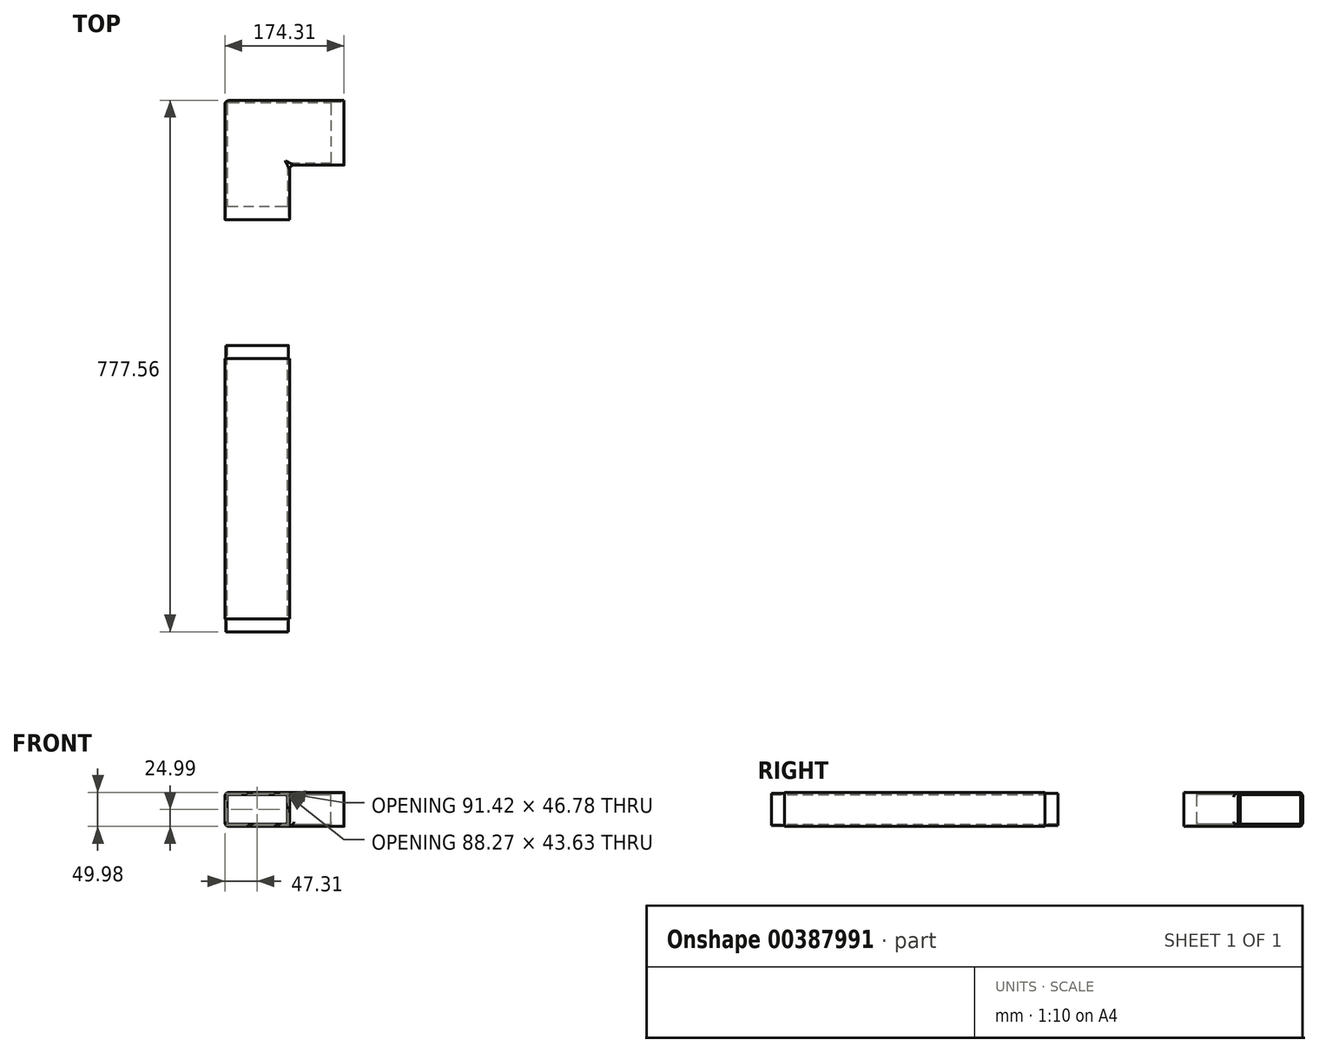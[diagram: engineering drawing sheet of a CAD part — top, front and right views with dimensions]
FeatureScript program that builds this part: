
annotation { "Feature Type Name" : "Feature", "Feature Type Description" : "" }
export const myFeature = defineFeature(function(context is Context, id is Id, definition is map)
    precondition{}
    {
        {
            var Q0;
            Q0=qCreatedBy(makeId("Front.planeOp"),FACE);
            var Q1;
            Q1=qCreatedBy(makeId("Right.planeOp"),FACE);
            cPlane(context, id + "F0", {"entities" : qUnion([Q0, Q1]), "cplaneType" : CPlaneType.MID_PLANE, "offset" : 25.4 * mm, "width" : 152.4 * mm, "height" : 152.4 * mm});
        }
        {
            var Q0;
            Q0=qCreatedBy(makeId("Right.planeOp"),FACE);
            cPlane(context, id + "F1", {"entities" : qUnion([Q0]), "cplaneType" : CPlaneType.OFFSET, "offset" : 127 * mm, "width" : 152.4 * mm, "height" : 152.4 * mm});
        }
        {
            var Q0;
            Q0=qCreatedBy(makeId("Front.planeOp"),FACE);
            cPlane(context, id + "F2", {"entities" : qUnion([Q0]), "cplaneType" : CPlaneType.OFFSET, "offset" : 127 * mm, "width" : 152.4 * mm, "height" : 152.4 * mm});
        }
        {
            var Q0;
            Q0=qCreatedBy(id+"F2.planeOp",FACE);
            var sketch = newSketch(context, id + "F3", { "sketchPlane" : qUnion([Q0])});
            skLineSegment(sketch, "E0.bottom", {"start": v(40.96, -24.99) * mm, "end": v(-40.96, -24.99) * mm});
            skLineSegment(sketch, "E0.top", {"start": v(40.96, 24.99) * mm, "end": v(-40.96, 24.99) * mm});
            skLineSegment(sketch, "E0.left", {"start": v(47.31, -18.64) * mm, "end": v(47.31, 18.64) * mm});
            skLineSegment(sketch, "E0.right", {"start": v(-47.31, -18.64) * mm, "end": v(-47.31, 18.64) * mm});
            skLineSegment(sketch, "E1.0", {"start": v(40.96, 21.81) * mm, "end": v(-40.96, 21.81) * mm});
            skLineSegment(sketch, "E1.1", {"start": v(44.14, -18.64) * mm, "end": v(44.14, 18.64) * mm});
            skLineSegment(sketch, "E1.2", {"start": v(40.96, -21.81) * mm, "end": v(-40.96, -21.81) * mm});
            skLineSegment(sketch, "E1.3", {"start": v(-44.14, -18.64) * mm, "end": v(-44.14, 18.64) * mm});
            skArc(sketch, "E2.filletArc", {"start": v(-40.96, 21.81) * mm, "mid": v(-43.2, 20.88) * mm, "end": v(-44.14, 18.64) * mm});
            skArc(sketch, "E3.filletArc", {"start": v(-44.14, -18.64) * mm, "mid": v(-43.2, -20.88) * mm, "end": v(-40.96, -21.81) * mm});
            skArc(sketch, "E4.filletArc", {"start": v(44.14, 18.64) * mm, "mid": v(43.2, 20.88) * mm, "end": v(40.96, 21.81) * mm});
            skArc(sketch, "E5.filletArc", {"start": v(40.96, -21.81) * mm, "mid": v(43.2, -20.88) * mm, "end": v(44.14, -18.64) * mm});
            skArc(sketch, "E6.filletArc", {"start": v(47.31, 18.64) * mm, "mid": v(45.45, 23.13) * mm, "end": v(40.96, 24.99) * mm});
            skArc(sketch, "E7.filletArc", {"start": v(40.96, -24.99) * mm, "mid": v(45.45, -23.13) * mm, "end": v(47.31, -18.64) * mm});
            skArc(sketch, "E8.filletArc", {"start": v(-47.31, -18.64) * mm, "mid": v(-45.45, -23.13) * mm, "end": v(-40.96, -24.99) * mm});
            skArc(sketch, "E9.filletArc", {"start": v(-40.96, 24.99) * mm, "mid": v(-45.45, 23.13) * mm, "end": v(-47.31, 18.64) * mm});
            skSolve(sketch);
        }
        {
            var Q0;
            Q0=qCreatedBy(id+"F1.planeOp",FACE);
            var sketch = newSketch(context, id + "F4", { "sketchPlane" : qUnion([Q0])});
            skLineSegment(sketch, "E10.bottom", {"start": v(40.96, -24.99) * mm, "end": v(-40.96, -24.99) * mm});
            skLineSegment(sketch, "E10.top", {"start": v(40.96, 24.99) * mm, "end": v(-40.96, 24.99) * mm});
            skLineSegment(sketch, "E10.left", {"start": v(47.31, -18.64) * mm, "end": v(47.31, 18.64) * mm});
            skLineSegment(sketch, "E10.right", {"start": v(-47.31, -18.64) * mm, "end": v(-47.31, 18.64) * mm});
            skLineSegment(sketch, "E11.0", {"start": v(40.96, 21.81) * mm, "end": v(-40.96, 21.81) * mm});
            skLineSegment(sketch, "E11.1", {"start": v(44.14, -18.64) * mm, "end": v(44.14, 18.64) * mm});
            skLineSegment(sketch, "E11.2", {"start": v(40.96, -21.81) * mm, "end": v(-40.96, -21.81) * mm});
            skLineSegment(sketch, "E11.3", {"start": v(-44.14, -18.64) * mm, "end": v(-44.14, 18.64) * mm});
            skArc(sketch, "E12.filletArc", {"start": v(-40.96, 21.81) * mm, "mid": v(-43.2, 20.88) * mm, "end": v(-44.14, 18.64) * mm});
            skArc(sketch, "E13.filletArc", {"start": v(-44.14, -18.64) * mm, "mid": v(-43.2, -20.88) * mm, "end": v(-40.96, -21.81) * mm});
            skArc(sketch, "E14.filletArc", {"start": v(44.14, 18.64) * mm, "mid": v(43.2, 20.88) * mm, "end": v(40.96, 21.81) * mm});
            skArc(sketch, "E15.filletArc", {"start": v(40.96, -21.81) * mm, "mid": v(43.2, -20.88) * mm, "end": v(44.14, -18.64) * mm});
            skArc(sketch, "E16.filletArc", {"start": v(47.31, 18.64) * mm, "mid": v(45.45, 23.13) * mm, "end": v(40.96, 24.99) * mm});
            skArc(sketch, "E17.filletArc", {"start": v(40.96, -24.99) * mm, "mid": v(45.45, -23.13) * mm, "end": v(47.31, -18.64) * mm});
            skArc(sketch, "E18.filletArc", {"start": v(-47.31, -18.64) * mm, "mid": v(-45.45, -23.13) * mm, "end": v(-40.96, -24.99) * mm});
            skArc(sketch, "E19.filletArc", {"start": v(-40.96, 24.99) * mm, "mid": v(-45.45, 23.13) * mm, "end": v(-47.31, 18.64) * mm});
            skSolve(sketch);
        }
        {
            var Q0;
            Q0 = qSketchRegion(id + "F3", true);
            var Q1;
            Q1=qCreatedBy(id+"F0.planeOp",FACE);
            extrude(context, id + "F5", {"entities" : qUnion([Q0]), "endBound" : BoundingType.UP_TO_SURFACE, "oppositeDirection" : true, "endBoundEntityFace" : qUnion([Q1]), "depth" : 25.4 * mm});
        }
        {
            var Q0;
            Q0 = qSketchRegion(id + "F4", true);
            var Q1;
            Q1=qCreatedBy(id+"F0.planeOp",FACE);
            extrude(context, id + "F6", {"entities" : qUnion([Q0]), "endBound" : BoundingType.UP_TO_SURFACE, "oppositeDirection" : true, "endBoundEntityFace" : qUnion([Q1]), "depth" : 25.4 * mm});
        }
        {
            var Q0;
            Q0=makeQuery(id+"F6.opExtrude","SWEPT_BODY",BODY,{"disambiguationData":[OSD([sQuery(id+"F4.wireOp",EDGE,"E10.bottom"),sQuery(id+"F4.wireOp",EDGE,"E10.top"),sQuery(id+"F4.wireOp",EDGE,"E10.left"),sQuery(id+"F4.wireOp",EDGE,"E10.right"),sQuery(id+"F4.wireOp",EDGE,"E11.0"),sQuery(id+"F4.wireOp",EDGE,"E11.1"),sQuery(id+"F4.wireOp",EDGE,"E11.2"),sQuery(id+"F4.wireOp",EDGE,"E11.3"),sQuery(id+"F4.wireOp",EDGE,"E12.filletArc"),sQuery(id+"F4.wireOp",EDGE,"E13.filletArc"),sQuery(id+"F4.wireOp",EDGE,"E14.filletArc"),sQuery(id+"F4.wireOp",EDGE,"E15.filletArc"),sQuery(id+"F4.wireOp",EDGE,"E16.filletArc"),sQuery(id+"F4.wireOp",EDGE,"E17.filletArc"),sQuery(id+"F4.wireOp",EDGE,"E18.filletArc"),sQuery(id+"F4.wireOp",EDGE,"E19.filletArc")])]});
            var Q1;
            Q1=makeQuery(id+"F5.opExtrude","SWEPT_BODY",BODY,{"disambiguationData":[OSD([sQuery(id+"F3.wireOp",EDGE,"E0.bottom"),sQuery(id+"F3.wireOp",EDGE,"E0.top"),sQuery(id+"F3.wireOp",EDGE,"E0.left"),sQuery(id+"F3.wireOp",EDGE,"E0.right"),sQuery(id+"F3.wireOp",EDGE,"E1.0"),sQuery(id+"F3.wireOp",EDGE,"E1.1"),sQuery(id+"F3.wireOp",EDGE,"E1.2"),sQuery(id+"F3.wireOp",EDGE,"E1.3"),sQuery(id+"F3.wireOp",EDGE,"E2.filletArc"),sQuery(id+"F3.wireOp",EDGE,"E3.filletArc"),sQuery(id+"F3.wireOp",EDGE,"E4.filletArc"),sQuery(id+"F3.wireOp",EDGE,"E5.filletArc"),sQuery(id+"F3.wireOp",EDGE,"E6.filletArc"),sQuery(id+"F3.wireOp",EDGE,"E7.filletArc"),sQuery(id+"F3.wireOp",EDGE,"E8.filletArc"),sQuery(id+"F3.wireOp",EDGE,"E9.filletArc")])]});
            booleanBodies(context, id + "F7", {"operationType" : BooleanOperationType.UNION, "tools" : qUnion([Q0, Q1])});
        }
        {
            var Q0;
            Q0=makeQuery(id+"F7.opBoolean","MERGE",EDGE,{"derivedFrom":[makeQuery(id+"F5.opExtrude","CAP_EDGE",EDGE,{"disambiguationData":[OSD([sQuery(id+"F3.wireOp",EDGE,"E0.right")])],"isStart":false}),makeQuery(id+"F6.opExtrude","CAP_EDGE",EDGE,{"disambiguationData":[OSD([sQuery(id+"F4.wireOp",EDGE,"E10.left")])],"isStart":false})]});
            fillet(context, id + "F8", {"entities" : qUnion([Q0]), "radius" : 6.35 * mm, "tangentPropagation" : true, "allowEdgeOverflow" : false});
        }
        {
            var Q0;
            Q0=makeQuery(id+"F7.opBoolean","MERGE",EDGE,{"derivedFrom":[makeQuery(id+"F5.opExtrude","CAP_EDGE",EDGE,{"disambiguationData":[OSD([sQuery(id+"F3.wireOp",EDGE,"E1.3")])],"isStart":false}),makeQuery(id+"F6.opExtrude","CAP_EDGE",EDGE,{"disambiguationData":[OSD([sQuery(id+"F4.wireOp",EDGE,"E11.1")])],"isStart":false})]});
            fillet(context, id + "F9", {"entities" : qUnion([Q0]), "radius" : 3.17 * mm, "tangentPropagation" : true, "allowEdgeOverflow" : false});
        }
        {
            var Q0;
            Q0=makeQuery(id+"F7.opBoolean","MERGE",EDGE,{"derivedFrom":[makeQuery(id+"F5.opExtrude","CAP_EDGE",EDGE,{"disambiguationData":[OSD([sQuery(id+"F3.wireOp",EDGE,"E0.left")])],"isStart":false}),makeQuery(id+"F6.opExtrude","CAP_EDGE",EDGE,{"disambiguationData":[OSD([sQuery(id+"F4.wireOp",EDGE,"E10.right")])],"isStart":false})]});
            fillet(context, id + "F10", {"entities" : qUnion([Q0]), "radius" : 6.35 * mm, "tangentPropagation" : true, "allowEdgeOverflow" : false});
        }
        {
            var Q0;
            Q0=makeQuery(id+"F7.opBoolean","MERGE",EDGE,{"derivedFrom":[makeQuery(id+"F5.opExtrude","CAP_EDGE",EDGE,{"disambiguationData":[OSD([sQuery(id+"F3.wireOp",EDGE,"E1.1")])],"isStart":false}),makeQuery(id+"F6.opExtrude","CAP_EDGE",EDGE,{"disambiguationData":[OSD([sQuery(id+"F4.wireOp",EDGE,"E11.3")])],"isStart":false})]});
            fillet(context, id + "F11", {"entities" : qUnion([Q0]), "radius" : 3.17 * mm, "tangentPropagation" : true, "allowEdgeOverflow" : false});
        }
        {
            var Q0;
            Q0=makeQuery(id+"F6.opExtrude","CAP_FACE",FACE,{"disambiguationData":[OSD([sQuery(id+"F4.wireOp",EDGE,"E10.bottom"),sQuery(id+"F4.wireOp",EDGE,"E10.top"),sQuery(id+"F4.wireOp",EDGE,"E10.left"),sQuery(id+"F4.wireOp",EDGE,"E10.right"),sQuery(id+"F4.wireOp",EDGE,"E11.0"),sQuery(id+"F4.wireOp",EDGE,"E11.1"),sQuery(id+"F4.wireOp",EDGE,"E11.2"),sQuery(id+"F4.wireOp",EDGE,"E11.3"),sQuery(id+"F4.wireOp",EDGE,"E12.filletArc"),sQuery(id+"F4.wireOp",EDGE,"E13.filletArc"),sQuery(id+"F4.wireOp",EDGE,"E14.filletArc"),sQuery(id+"F4.wireOp",EDGE,"E15.filletArc"),sQuery(id+"F4.wireOp",EDGE,"E16.filletArc"),sQuery(id+"F4.wireOp",EDGE,"E17.filletArc"),sQuery(id+"F4.wireOp",EDGE,"E18.filletArc"),sQuery(id+"F4.wireOp",EDGE,"E19.filletArc")])],"isStart":true});
            var sketch = newSketch(context, id + "F12", { "sketchPlane" : qUnion([Q0])});
            skLineSegment(sketch, "E20.0", {"start": v(40.96, 21.81) * mm, "end": v(-40.96, 21.81) * mm});
            skLineSegment(sketch, "E20.1", {"start": v(44.14, -18.64) * mm, "end": v(44.14, 18.64) * mm});
            skLineSegment(sketch, "E20.2", {"start": v(40.96, -21.81) * mm, "end": v(-40.96, -21.81) * mm});
            skLineSegment(sketch, "E20.3", {"start": v(-44.14, -18.64) * mm, "end": v(-44.14, 18.64) * mm});
            skArc(sketch, "E21.filletArc", {"start": v(-40.96, 21.81) * mm, "mid": v(-43.2, 20.88) * mm, "end": v(-44.14, 18.64) * mm});
            skArc(sketch, "E22.filletArc", {"start": v(-44.14, -18.64) * mm, "mid": v(-43.2, -20.88) * mm, "end": v(-40.96, -21.81) * mm});
            skArc(sketch, "E23.filletArc", {"start": v(44.14, 18.64) * mm, "mid": v(43.2, 20.88) * mm, "end": v(40.96, 21.81) * mm});
            skArc(sketch, "E24.filletArc", {"start": v(40.96, -21.81) * mm, "mid": v(43.2, -20.88) * mm, "end": v(44.14, -18.64) * mm});
            skArc(sketch, "E25.0", {"start": v(45.71, 18.64) * mm, "mid": v(44.32, 22) * mm, "end": v(40.96, 23.39) * mm});
            skLineSegment(sketch, "E25.1", {"start": v(45.71, -18.64) * mm, "end": v(45.71, 18.64) * mm});
            skLineSegment(sketch, "E25.2", {"start": v(40.96, 23.39) * mm, "end": v(-40.96, 23.39) * mm});
            skArc(sketch, "E25.3", {"start": v(40.96, -23.39) * mm, "mid": v(44.32, -22) * mm, "end": v(45.71, -18.64) * mm});
            skArc(sketch, "E25.4", {"start": v(-40.96, 23.39) * mm, "mid": v(-44.32, 22) * mm, "end": v(-45.71, 18.64) * mm});
            skLineSegment(sketch, "E25.5", {"start": v(-45.71, -18.64) * mm, "end": v(-45.71, 18.64) * mm});
            skArc(sketch, "E25.6", {"start": v(-45.71, -18.64) * mm, "mid": v(-44.32, -22) * mm, "end": v(-40.96, -23.39) * mm});
            skLineSegment(sketch, "E25.7", {"start": v(40.96, -23.39) * mm, "end": v(-40.96, -23.39) * mm});
            skSolve(sketch);
        }
        {
            var Q0;
            Q0=makeQuery(id+"F12.imprint","IMPRINT",FACE,{"disambiguationData":[TD([[makeQuery(id+"F12.imprint","IMPRINT",EDGE,{"derivedFrom":sQuery(id+"F12.wireOp",EDGE,"E20.0")}),-1.0]])]});
            var Q1;
            Q1=sQuery(id+"F12.wireOp",EDGE,"E20.0");
            var Q2;
            Q2=sQuery(id+"F12.wireOp",EDGE,"E20.1");
            var Q3;
            Q3=sQuery(id+"F12.wireOp",EDGE,"E20.2");
            var Q4;
            Q4=sQuery(id+"F12.wireOp",EDGE,"E20.3");
            var Q5;
            Q5=sQuery(id+"F12.wireOp",EDGE,"E21.filletArc");
            var Q6;
            Q6=sQuery(id+"F12.wireOp",EDGE,"E22.filletArc");
            var Q7;
            Q7=sQuery(id+"F12.wireOp",EDGE,"E23.filletArc");
            var Q8;
            Q8=sQuery(id+"F12.wireOp",EDGE,"E24.filletArc");
            var Q9;
            Q9=sQuery(id+"F12.wireOp",EDGE,"E25.0");
            var Q10;
            Q10=sQuery(id+"F12.wireOp",EDGE,"E25.1");
            var Q11;
            Q11=sQuery(id+"F12.wireOp",EDGE,"E25.2");
            var Q12;
            Q12=sQuery(id+"F12.wireOp",EDGE,"E25.3");
            var Q13;
            Q13=sQuery(id+"F12.wireOp",EDGE,"E25.4");
            var Q14;
            Q14=sQuery(id+"F12.wireOp",EDGE,"E25.5");
            var Q15;
            Q15=sQuery(id+"F12.wireOp",EDGE,"E25.6");
            var Q16;
            Q16=sQuery(id+"F12.wireOp",EDGE,"E25.7");
            extrude(context, id + "F13", {"entities" : qUnion([Q0]), "operationType" : NewBodyOperationType.REMOVE, "surfaceEntities" : qUnion([Q1, Q2, Q3, Q4, Q5, Q6, Q7, Q8, Q9, Q10, Q11, Q12, Q13, Q14, Q15, Q16]), "oppositeDirection" : true, "depth" : 19.05 * mm});
        }
        {
            var Q0;
            Q0=makeQuery(id+"F5.opExtrude","CAP_FACE",FACE,{"disambiguationData":[OSD([sQuery(id+"F3.wireOp",EDGE,"E0.bottom"),sQuery(id+"F3.wireOp",EDGE,"E0.top"),sQuery(id+"F3.wireOp",EDGE,"E0.left"),sQuery(id+"F3.wireOp",EDGE,"E0.right"),sQuery(id+"F3.wireOp",EDGE,"E1.0"),sQuery(id+"F3.wireOp",EDGE,"E1.1"),sQuery(id+"F3.wireOp",EDGE,"E1.2"),sQuery(id+"F3.wireOp",EDGE,"E1.3"),sQuery(id+"F3.wireOp",EDGE,"E2.filletArc"),sQuery(id+"F3.wireOp",EDGE,"E3.filletArc"),sQuery(id+"F3.wireOp",EDGE,"E4.filletArc"),sQuery(id+"F3.wireOp",EDGE,"E5.filletArc"),sQuery(id+"F3.wireOp",EDGE,"E6.filletArc"),sQuery(id+"F3.wireOp",EDGE,"E7.filletArc"),sQuery(id+"F3.wireOp",EDGE,"E8.filletArc"),sQuery(id+"F3.wireOp",EDGE,"E9.filletArc")])],"isStart":true});
            var sketch = newSketch(context, id + "F14", { "sketchPlane" : qUnion([Q0])});
            skArc(sketch, "E26.0", {"start": v(45.71, 18.64) * mm, "mid": v(44.32, 22) * mm, "end": v(40.96, 23.39) * mm});
            skLineSegment(sketch, "E26.1", {"start": v(45.71, -18.64) * mm, "end": v(45.71, 18.64) * mm});
            skLineSegment(sketch, "E26.2", {"start": v(40.96, 23.39) * mm, "end": v(-40.96, 23.39) * mm});
            skArc(sketch, "E26.3", {"start": v(40.96, -23.39) * mm, "mid": v(44.32, -22) * mm, "end": v(45.71, -18.64) * mm});
            skArc(sketch, "E26.4", {"start": v(-40.96, 23.39) * mm, "mid": v(-44.32, 22) * mm, "end": v(-45.71, 18.64) * mm});
            skLineSegment(sketch, "E26.5", {"start": v(-45.71, -18.64) * mm, "end": v(-45.71, 18.64) * mm});
            skArc(sketch, "E26.6", {"start": v(-45.71, -18.64) * mm, "mid": v(-44.32, -22) * mm, "end": v(-40.96, -23.39) * mm});
            skLineSegment(sketch, "E26.7", {"start": v(40.96, -23.39) * mm, "end": v(-40.96, -23.39) * mm});
            skSolve(sketch);
        }
        {
            var Q0;
            Q0=makeQuery(id+"F14.imprint","IMPRINT",FACE,{"disambiguationData":[TD([[makeQuery(id+"F14.imprint","IMPRINT",EDGE,{"derivedFrom":sQuery(id+"F14.wireOp",EDGE,"E26.0")}),1.0]])]});
            extrude(context, id + "F15", {"entities" : qUnion([Q0]), "operationType" : NewBodyOperationType.REMOVE, "oppositeDirection" : true, "depth" : 19.05 * mm});
        }
        {
            var Q0;
            Q0=qCreatedBy(id+"F2.planeOp",FACE);
            cPlane(context, id + "F16", {"entities" : qUnion([Q0]), "cplaneType" : CPlaneType.OFFSET, "offset" : 203.2 * mm, "width" : 152.4 * mm, "height" : 152.4 * mm});
        }
        {
            var Q0;
            Q0=qCreatedBy(id+"F16.planeOp",FACE);
            var sketch = newSketch(context, id + "F17", { "sketchPlane" : qUnion([Q0])});
            skLineSegment(sketch, "E27.bottom", {"start": v(40.96, -24.99) * mm, "end": v(-40.96, -24.99) * mm});
            skLineSegment(sketch, "E27.top", {"start": v(40.96, 24.99) * mm, "end": v(-40.96, 24.99) * mm});
            skLineSegment(sketch, "E27.left", {"start": v(47.31, -18.64) * mm, "end": v(47.31, 18.64) * mm});
            skLineSegment(sketch, "E27.right", {"start": v(-47.31, -18.64) * mm, "end": v(-47.31, 18.64) * mm});
            skLineSegment(sketch, "E28.0", {"start": v(40.96, 21.81) * mm, "end": v(-40.96, 21.81) * mm});
            skLineSegment(sketch, "E28.1", {"start": v(44.14, -18.64) * mm, "end": v(44.14, 18.64) * mm});
            skLineSegment(sketch, "E28.2", {"start": v(40.96, -21.81) * mm, "end": v(-40.96, -21.81) * mm});
            skLineSegment(sketch, "E28.3", {"start": v(-44.14, -18.64) * mm, "end": v(-44.14, 18.64) * mm});
            skArc(sketch, "E29.filletArc", {"start": v(-40.96, 21.81) * mm, "mid": v(-43.2, 20.88) * mm, "end": v(-44.14, 18.64) * mm});
            skArc(sketch, "E30.filletArc", {"start": v(-44.14, -18.64) * mm, "mid": v(-43.2, -20.88) * mm, "end": v(-40.96, -21.81) * mm});
            skArc(sketch, "E31.filletArc", {"start": v(44.14, 18.64) * mm, "mid": v(43.2, 20.88) * mm, "end": v(40.96, 21.81) * mm});
            skArc(sketch, "E32.filletArc", {"start": v(40.96, -21.81) * mm, "mid": v(43.2, -20.88) * mm, "end": v(44.14, -18.64) * mm});
            skArc(sketch, "E33.filletArc", {"start": v(47.31, 18.64) * mm, "mid": v(45.45, 23.13) * mm, "end": v(40.96, 24.99) * mm});
            skArc(sketch, "E34.filletArc", {"start": v(40.96, -24.99) * mm, "mid": v(45.45, -23.13) * mm, "end": v(47.31, -18.64) * mm});
            skArc(sketch, "E35.filletArc", {"start": v(-47.31, -18.64) * mm, "mid": v(-45.45, -23.13) * mm, "end": v(-40.96, -24.99) * mm});
            skArc(sketch, "E36.filletArc", {"start": v(-40.96, 24.99) * mm, "mid": v(-45.45, 23.13) * mm, "end": v(-47.31, 18.64) * mm});
            skSolve(sketch);
        }
        {
            var Q0;
            Q0 = qSketchRegion(id + "F17", true);
            extrude(context, id + "F18", {"entities" : qUnion([Q0]), "depth" : 381 * mm});
        }
        {
            var Q0;
            Q0=qCreatedBy(id+"F16.planeOp",FACE);
            var sketch = newSketch(context, id + "F19", { "sketchPlane" : qUnion([Q0])});
            skLineSegment(sketch, "E37.0", {"start": v(40.94, 22) * mm, "end": v(-40.98, 22) * mm});
            skLineSegment(sketch, "E37.1", {"start": v(44.12, -18.44) * mm, "end": v(44.12, 18.83) * mm});
            skLineSegment(sketch, "E37.2", {"start": v(40.94, -21.62) * mm, "end": v(-40.98, -21.62) * mm});
            skLineSegment(sketch, "E37.3", {"start": v(-44.16, -18.44) * mm, "end": v(-44.16, 18.83) * mm});
            skArc(sketch, "E38.filletArc", {"start": v(-40.98, 22) * mm, "mid": v(-43.23, 21.08) * mm, "end": v(-44.16, 18.83) * mm});
            skArc(sketch, "E39.filletArc", {"start": v(-44.16, -18.44) * mm, "mid": v(-43.23, -20.69) * mm, "end": v(-40.98, -21.62) * mm});
            skArc(sketch, "E40.filletArc", {"start": v(44.12, 18.83) * mm, "mid": v(43.19, 21.08) * mm, "end": v(40.94, 22) * mm});
            skArc(sketch, "E41.filletArc", {"start": v(40.94, -21.62) * mm, "mid": v(43.19, -20.69) * mm, "end": v(44.12, -18.44) * mm});
            skArc(sketch, "E42.0", {"start": v(45.7, 18.83) * mm, "mid": v(44.3, 22.19) * mm, "end": v(40.94, 23.58) * mm});
            skLineSegment(sketch, "E42.1", {"start": v(45.7, -18.44) * mm, "end": v(45.7, 18.83) * mm});
            skLineSegment(sketch, "E42.2", {"start": v(40.94, 23.58) * mm, "end": v(-40.98, 23.58) * mm});
            skArc(sketch, "E42.3", {"start": v(40.94, -23.2) * mm, "mid": v(44.3, -21.8) * mm, "end": v(45.7, -18.44) * mm});
            skArc(sketch, "E42.4", {"start": v(-40.98, 23.58) * mm, "mid": v(-44.34, 22.19) * mm, "end": v(-45.73, 18.83) * mm});
            skLineSegment(sketch, "E42.5", {"start": v(-45.73, -18.44) * mm, "end": v(-45.73, 18.83) * mm});
            skArc(sketch, "E42.6", {"start": v(-45.73, -18.44) * mm, "mid": v(-44.34, -21.8) * mm, "end": v(-40.98, -23.2) * mm});
            skLineSegment(sketch, "E42.7", {"start": v(40.94, -23.2) * mm, "end": v(-40.98, -23.2) * mm});
            skSolve(sketch);
        }
        {
            var Q0;
            Q0=makeQuery(id+"F19.imprint","IMPRINT",FACE,{"disambiguationData":[TD([[makeQuery(id+"F19.imprint","IMPRINT",EDGE,{"derivedFrom":sQuery(id+"F19.wireOp",EDGE,"E37.0")}),-1.0]])]});
            extrude(context, id + "F20", {"entities" : qUnion([Q0]), "operationType" : NewBodyOperationType.ADD, "oppositeDirection" : true, "depth" : 19.05 * mm});
        }
        {
            var Q0;
            Q0=makeQuery(id+"F18.opExtrude","CAP_FACE",FACE,{"disambiguationData":[OSD([sQuery(id+"F17.wireOp",EDGE,"E27.bottom"),sQuery(id+"F17.wireOp",EDGE,"E27.top"),sQuery(id+"F17.wireOp",EDGE,"E27.left"),sQuery(id+"F17.wireOp",EDGE,"E27.right"),sQuery(id+"F17.wireOp",EDGE,"E28.0"),sQuery(id+"F17.wireOp",EDGE,"E28.1"),sQuery(id+"F17.wireOp",EDGE,"E28.2"),sQuery(id+"F17.wireOp",EDGE,"E28.3"),sQuery(id+"F17.wireOp",EDGE,"E29.filletArc"),sQuery(id+"F17.wireOp",EDGE,"E30.filletArc"),sQuery(id+"F17.wireOp",EDGE,"E31.filletArc"),sQuery(id+"F17.wireOp",EDGE,"E32.filletArc"),sQuery(id+"F17.wireOp",EDGE,"E33.filletArc"),sQuery(id+"F17.wireOp",EDGE,"E34.filletArc"),sQuery(id+"F17.wireOp",EDGE,"E35.filletArc"),sQuery(id+"F17.wireOp",EDGE,"E36.filletArc")])],"isStart":false});
            var sketch = newSketch(context, id + "F21", { "sketchPlane" : qUnion([Q0])});
            skLineSegment(sketch, "E43.0", {"start": v(40.96, 21.81) * mm, "end": v(-40.96, 21.81) * mm});
            skLineSegment(sketch, "E43.1", {"start": v(44.14, -18.64) * mm, "end": v(44.14, 18.64) * mm});
            skLineSegment(sketch, "E43.2", {"start": v(40.96, -21.81) * mm, "end": v(-40.96, -21.81) * mm});
            skLineSegment(sketch, "E43.3", {"start": v(-44.14, -18.64) * mm, "end": v(-44.14, 18.64) * mm});
            skArc(sketch, "E44.filletArc", {"start": v(-40.96, 21.81) * mm, "mid": v(-43.2, 20.88) * mm, "end": v(-44.14, 18.64) * mm});
            skArc(sketch, "E45.filletArc", {"start": v(-44.14, -18.64) * mm, "mid": v(-43.2, -20.88) * mm, "end": v(-40.96, -21.81) * mm});
            skArc(sketch, "E46.filletArc", {"start": v(44.14, 18.64) * mm, "mid": v(43.2, 20.88) * mm, "end": v(40.96, 21.81) * mm});
            skArc(sketch, "E47.filletArc", {"start": v(40.96, -21.81) * mm, "mid": v(43.2, -20.88) * mm, "end": v(44.14, -18.64) * mm});
            skArc(sketch, "E48.0", {"start": v(45.71, 18.64) * mm, "mid": v(44.32, 22) * mm, "end": v(40.96, 23.39) * mm});
            skLineSegment(sketch, "E48.1", {"start": v(45.71, -18.64) * mm, "end": v(45.71, 18.64) * mm});
            skLineSegment(sketch, "E48.2", {"start": v(40.96, 23.39) * mm, "end": v(-40.96, 23.39) * mm});
            skArc(sketch, "E48.3", {"start": v(40.96, -23.39) * mm, "mid": v(44.32, -22) * mm, "end": v(45.71, -18.64) * mm});
            skArc(sketch, "E48.4", {"start": v(-40.96, 23.39) * mm, "mid": v(-44.32, 22) * mm, "end": v(-45.71, 18.64) * mm});
            skLineSegment(sketch, "E48.5", {"start": v(-45.71, -18.64) * mm, "end": v(-45.71, 18.64) * mm});
            skArc(sketch, "E48.6", {"start": v(-45.71, -18.64) * mm, "mid": v(-44.32, -22) * mm, "end": v(-40.96, -23.39) * mm});
            skLineSegment(sketch, "E48.7", {"start": v(40.96, -23.39) * mm, "end": v(-40.96, -23.39) * mm});
            skSolve(sketch);
        }
        {
            var Q0;
            Q0=makeQuery(id+"F21.imprint","IMPRINT",FACE,{"disambiguationData":[TD([[makeQuery(id+"F21.imprint","IMPRINT",EDGE,{"derivedFrom":sQuery(id+"F21.wireOp",EDGE,"E43.0")}),-1.0]])]});
            extrude(context, id + "F22", {"entities" : qUnion([Q0]), "operationType" : NewBodyOperationType.ADD, "depth" : 19.05 * mm});
        }
    });
